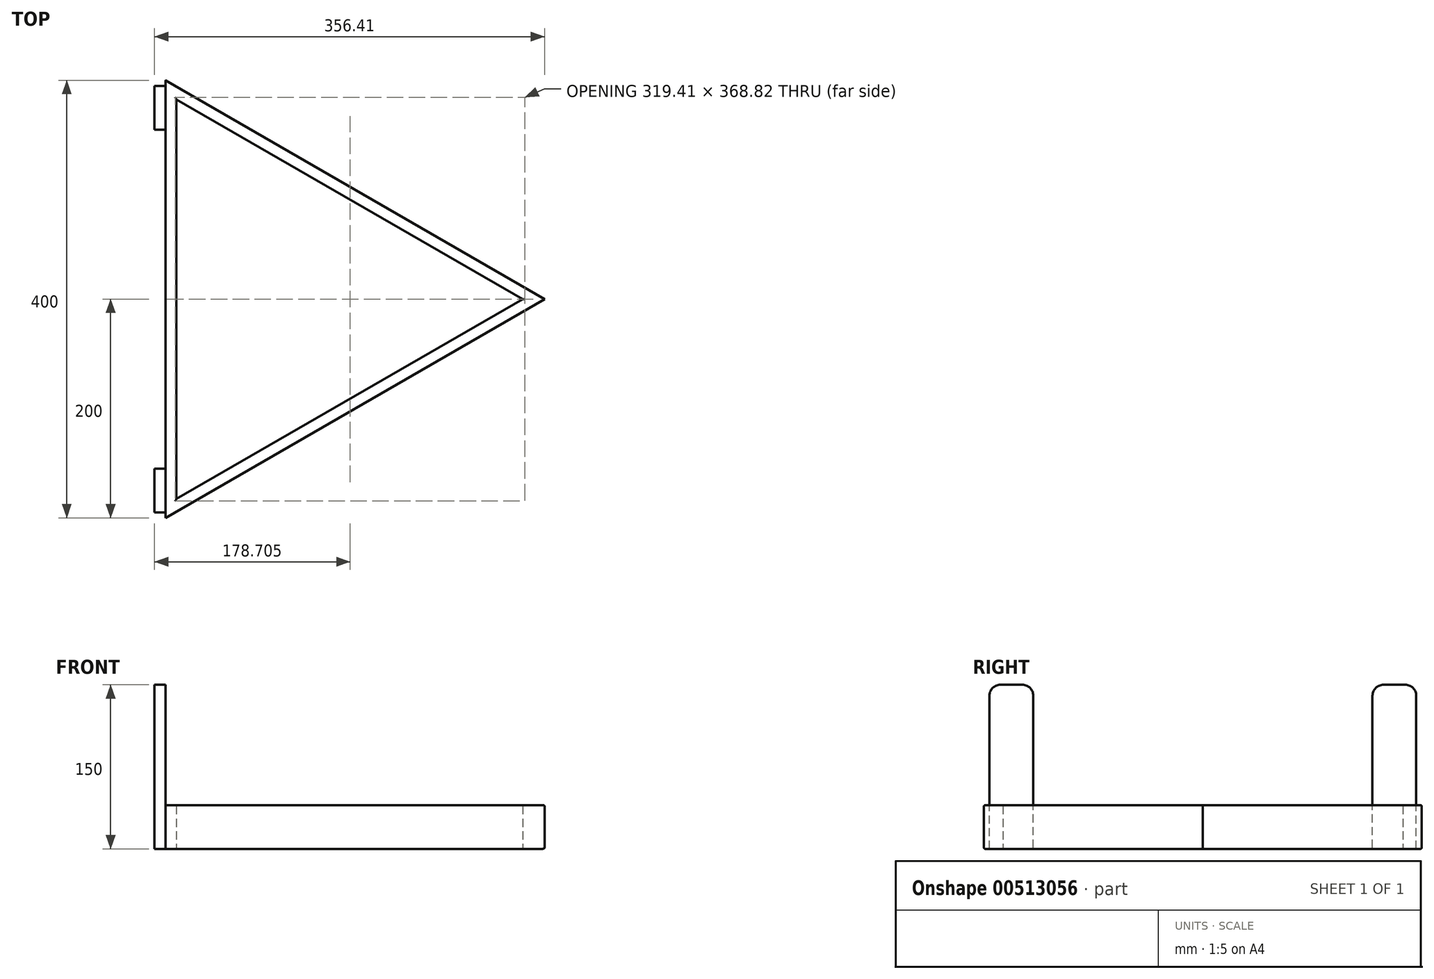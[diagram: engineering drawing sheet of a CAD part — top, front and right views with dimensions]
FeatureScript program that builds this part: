
annotation { "Feature Type Name" : "Feature", "Feature Type Description" : "" }
export const myFeature = defineFeature(function(context is Context, id is Id, definition is map)
    precondition{}
    {
        {
            var Q0;
            Q0=qCreatedBy(makeId("Top.planeOp"),FACE);
            var sketch = newSketch(context, id + "F0", { "sketchPlane" : qUnion([Q0])});
            skLineSegment(sketch, "E0", {"start": v(0, 0) * mm, "end": v(-346.41, 200) * mm});
            skLineSegment(sketch, "E1", {"start": v(-346.41, 200) * mm, "end": v(-346.41, -200) * mm});
            skLineSegment(sketch, "E2", {"start": v(-346.41, -200) * mm, "end": v(0, 0) * mm});
            skLineSegment(sketch, "E3", {"start": v(-20, 0) * mm, "end": v(-336.41, 182.68) * mm});
            skLineSegment(sketch, "E4", {"start": v(-336.41, 182.68) * mm, "end": v(-336.41, -182.68) * mm});
            skLineSegment(sketch, "E5", {"start": v(-336.41, -182.68) * mm, "end": v(-20, 0) * mm});
            skSolve(sketch);
        }
        {
            var Q0;
            Q0 = qSketchRegion(id + "F0", true);
            extrude(context, id + "F1", {"entities" : qUnion([Q0]), "depth" : 40 * mm});
        }
        {
            var Q0;
            Q0=makeQuery(id+"F1.opExtrude","SWEPT_FACE",FACE,{"disambiguationData":[OSD([sQuery(id+"F0.wireOp",EDGE,"E1")])]});
            var sketch = newSketch(context, id + "F2", { "sketchPlane" : qUnion([Q0])});
            skLineSegment(sketch, "E6.bottom", {"start": v(-195, 0) * mm, "end": v(-155, 0) * mm});
            skLineSegment(sketch, "E6.top", {"start": v(-185, 150) * mm, "end": v(-165, 150) * mm});
            skLineSegment(sketch, "E6.left", {"start": v(-195, 0) * mm, "end": v(-195, 140) * mm});
            skLineSegment(sketch, "E6.right", {"start": v(-155, 0) * mm, "end": v(-155, 140) * mm});
            skLineSegment(sketch, "E7.bottom", {"start": v(195, 0) * mm, "end": v(155, 0) * mm});
            skLineSegment(sketch, "E7.top", {"start": v(185, 150) * mm, "end": v(165, 150) * mm});
            skLineSegment(sketch, "E7.left", {"start": v(195, 0) * mm, "end": v(195, 140) * mm});
            skLineSegment(sketch, "E7.right", {"start": v(155, 0) * mm, "end": v(155, 140) * mm});
            skPoint(sketch, "E8.visualSharp", {"position": v(-195, 150) * mm});
            skArc(sketch, "E8.filletArc", {"start": v(-185, 150) * mm, "mid": v(-192.07, 147.07) * mm, "end": v(-195, 140) * mm});
            skPoint(sketch, "E9.visualSharp", {"position": v(-155, 150) * mm});
            skArc(sketch, "E9.filletArc", {"start": v(-155, 140) * mm, "mid": v(-157.93, 147.07) * mm, "end": v(-165, 150) * mm});
            skPoint(sketch, "E10.visualSharp", {"position": v(155, 150) * mm});
            skArc(sketch, "E10.filletArc", {"start": v(165, 150) * mm, "mid": v(157.93, 147.07) * mm, "end": v(155, 140) * mm});
            skPoint(sketch, "E11.visualSharp", {"position": v(195, 150) * mm});
            skArc(sketch, "E11.filletArc", {"start": v(195, 140) * mm, "mid": v(192.07, 147.07) * mm, "end": v(185, 150) * mm});
            skSolve(sketch);
        }
        {
            var Q0;
            Q0 = qSketchRegion(id + "F2", true);
            extrude(context, id + "F3", {"entities" : qUnion([Q0]), "operationType" : NewBodyOperationType.ADD, "depth" : 10 * mm});
        }
        {
            var Q0;
            {var subQ0=sQuery(id+"F2.wireOp",EDGE,"E6.right");var subQ1=sQuery(id+"F0.wireOp",EDGE,"E1");var subQ2=makeQuery(id+"F1.opExtrude","SWEPT_FACE",FACE,{"disambiguationData":[OSD([subQ1])]});var subQ3=makeQuery(id+"F1.opExtrude","CAP_FACE",FACE,{"disambiguationData":[OSD([sQuery(id+"F0.wireOp",EDGE,"E0"),subQ1,sQuery(id+"F0.wireOp",EDGE,"E2"),sQuery(id+"F0.wireOp",EDGE,"E3"),sQuery(id+"F0.wireOp",EDGE,"E4"),sQuery(id+"F0.wireOp",EDGE,"E5")])],"isStart":false});Q0=makeQuery(id+"F3.boolean.opBoolean","SPLIT",EDGE,{"disambiguationData":[topologyDisambiguationEdgeConnected([subQ3,subQ2]),TD([makeQuery(id+"F3.opExtrude","SWEPT_FACE",FACE,{"disambiguationData":[OSD([subQ0])]})])],"derivedFrom":makeQuery(id+"F1.opExtrude","CAP_EDGE",EDGE,{"disambiguationData":[OSD([subQ1])],"isStart":false})});}
            var Q1;
            Q1=makeQuery(id+"F1.opExtrude","CAP_EDGE",EDGE,{"disambiguationData":[OSD([sQuery(id+"F0.wireOp",EDGE,"E3")])],"isStart":false});
            var Q2;
            Q2=makeQuery(id+"F1.opExtrude","CAP_EDGE",EDGE,{"disambiguationData":[OSD([sQuery(id+"F0.wireOp",EDGE,"E0")])],"isStart":false});
            var Q3;
            Q3=makeQuery(id+"F1.opExtrude","CAP_EDGE",EDGE,{"disambiguationData":[OSD([sQuery(id+"F0.wireOp",EDGE,"E2")])],"isStart":false});
            var Q4;
            Q4=makeQuery(id+"F1.opExtrude","CAP_EDGE",EDGE,{"disambiguationData":[OSD([sQuery(id+"F0.wireOp",EDGE,"E5")])],"isStart":false});
            var Q5;
            Q5=makeQuery(id+"F1.opExtrude","CAP_EDGE",EDGE,{"disambiguationData":[OSD([sQuery(id+"F0.wireOp",EDGE,"E4")])],"isStart":false});
            var Q6;
            Q6=makeQuery(id+"F1.opExtrude","CAP_EDGE",EDGE,{"disambiguationData":[OSD([sQuery(id+"F0.wireOp",EDGE,"E2")])],"isStart":true});
            var Q7;
            Q7=makeQuery(id+"F1.opExtrude","CAP_EDGE",EDGE,{"disambiguationData":[OSD([sQuery(id+"F0.wireOp",EDGE,"E0")])],"isStart":true});
            var Q8;
            {var subQ0=sQuery(id+"F0.wireOp",EDGE,"E1");Q8=makeQuery(id+"F3.boolean.opBoolean","SPLIT",EDGE,{"disambiguationData":[TD([makeQuery(id+"F3.opExtrude","SWEPT_FACE",FACE,{"disambiguationData":[OSD([sQuery(id+"F2.wireOp",EDGE,"E6.right")])]})])],"derivedFrom":makeQuery(id+"F1.opExtrude","CAP_EDGE",EDGE,{"disambiguationData":[OSD([subQ0])],"isStart":true})});}
            var Q9;
            Q9=makeQuery(id+"F1.opExtrude","CAP_EDGE",EDGE,{"disambiguationData":[OSD([sQuery(id+"F0.wireOp",EDGE,"E5")])],"isStart":true});
            var Q10;
            Q10=makeQuery(id+"F1.opExtrude","CAP_EDGE",EDGE,{"disambiguationData":[OSD([sQuery(id+"F0.wireOp",EDGE,"E3")])],"isStart":true});
            var Q11;
            Q11=makeQuery(id+"F1.opExtrude","CAP_EDGE",EDGE,{"disambiguationData":[OSD([sQuery(id+"F0.wireOp",EDGE,"E4")])],"isStart":true});
            fillet(context, id + "F4", {"entities" : qUnion([Q0, Q1, Q2, Q3, Q4, Q5, Q6, Q7, Q8, Q9, Q10, Q11]), "radius" : 1 * mm, "tangentPropagation" : true, "allowEdgeOverflow" : false});
        }
    });
